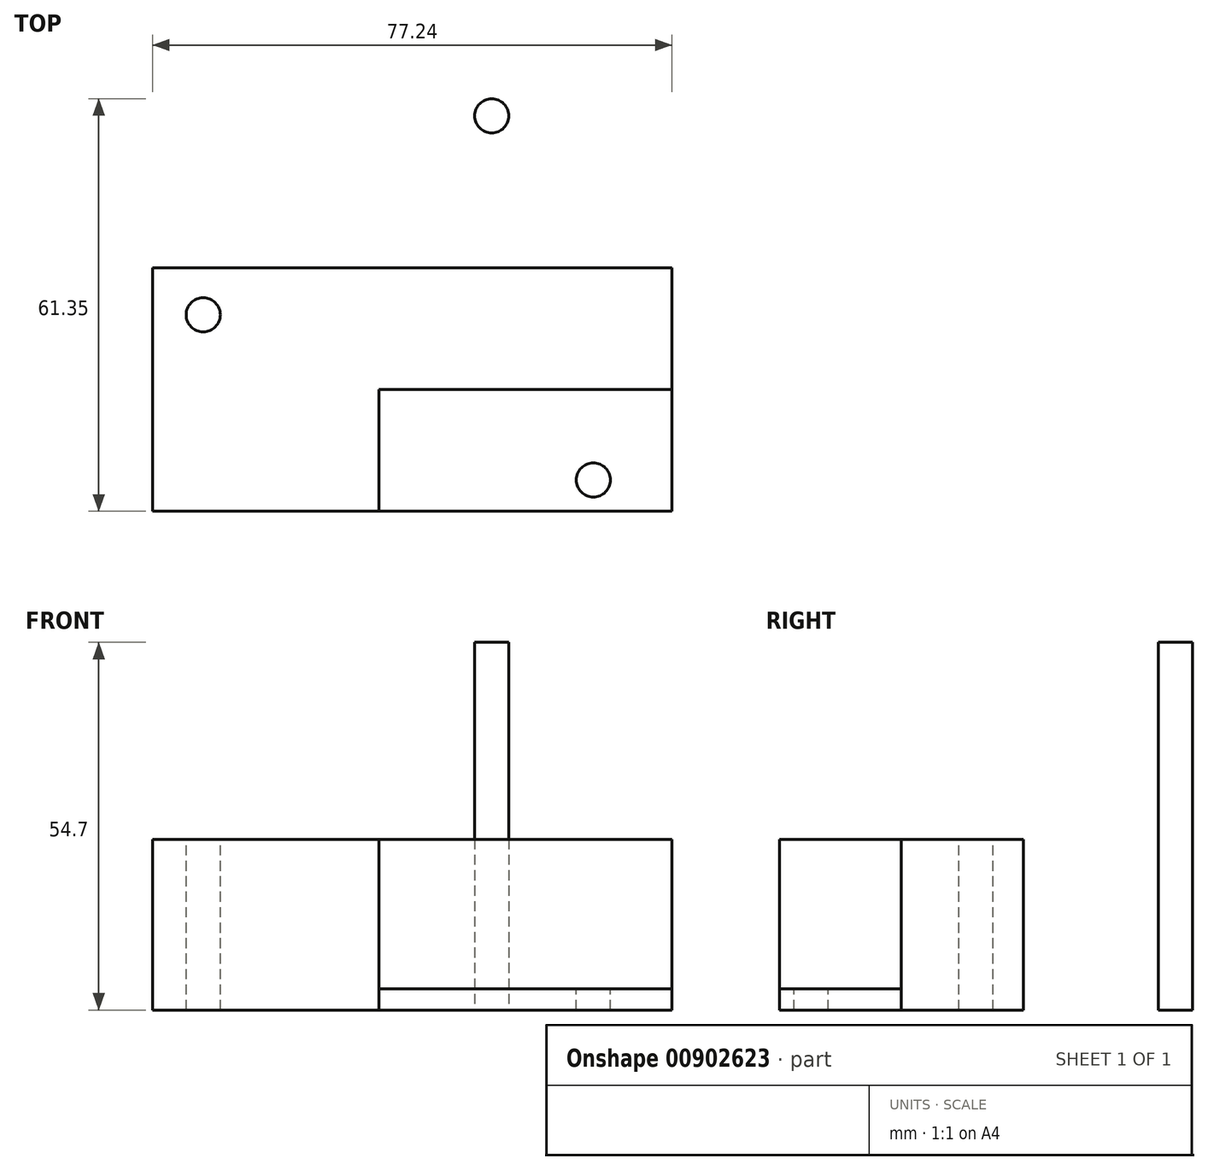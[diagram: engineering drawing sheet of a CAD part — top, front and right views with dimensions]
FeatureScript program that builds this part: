
annotation { "Feature Type Name" : "Feature", "Feature Type Description" : "" }
export const myFeature = defineFeature(function(context is Context, id is Id, definition is map)
    precondition{}
    {
        {
            var Q0;
            Q0=qCreatedBy(makeId("Top.planeOp"),FACE);
            var sketch = newSketch(context, id + "F0", { "sketchPlane" : qUnion([Q0])});
            skLineSegment(sketch, "E0.bottom", {"start": v(0, 0) * mm, "end": v(-77.24, 0) * mm});
            skLineSegment(sketch, "E0.top", {"start": v(0, 36.22) * mm, "end": v(-77.24, 36.22) * mm});
            skLineSegment(sketch, "E0.left", {"start": v(0, 0) * mm, "end": v(0, 36.22) * mm});
            skLineSegment(sketch, "E0.right", {"start": v(-77.24, 0) * mm, "end": v(-77.24, 36.22) * mm});
            skPoint(sketch, "E1.oppositeSnap0", {"position": v(0, 18.1) * mm});
            skLineSegment(sketch, "E1.bottom", {"start": v(0, 0) * mm, "end": v(-43.6, 0) * mm});
            skLineSegment(sketch, "E1.top", {"start": v(0, 18.1) * mm, "end": v(-43.6, 18.1) * mm});
            skLineSegment(sketch, "E1.left", {"start": v(0, 0) * mm, "end": v(0, 18.1) * mm});
            skLineSegment(sketch, "E1.right", {"start": v(-43.6, 0) * mm, "end": v(-43.6, 18.1) * mm});
            skSolve(sketch);
        }
        {
            var Q0;
            {var subQ2=sQuery(id+"F0.wireOp",EDGE,"E0.top");Q0=makeQuery(id+"F0.imprint","IMPRINT",FACE,{"disambiguationData":[TD([[makeQuery(id+"F0.imprint","IMPRINT",EDGE,{"derivedFrom":subQ2}),1.0]])]});}
            extrude(context, id + "F1", {"entities" : qUnion([Q0]), "depth" : 25.4 * mm, "offsetDistance" : 25.4 * mm});
        }
        {
            var Q0;
            {var subQ4=sQuery(id+"F0.wireOp",EDGE,"E1.top");Q0=makeQuery(id+"F0.imprint","IMPRINT",FACE,{"disambiguationData":[TD([[makeQuery(id+"F0.imprint","IMPRINT",EDGE,{"derivedFrom":subQ4}),1.0]])]});}
            extrude(context, id + "F2", {"entities" : qUnion([Q0]), "depth" : 3.12 * mm, "offsetDistance" : 25.4 * mm});
        }
        {
            var Q0;
            Q0=makeQuery(id+"F1.opExtrude","CAP_FACE",FACE,{"disambiguationData":[OSD([sQuery(id+"F0.wireOp",EDGE,"E0.bottom"),sQuery(id+"F0.wireOp",EDGE,"E0.top"),sQuery(id+"F0.wireOp",EDGE,"E0.left"),sQuery(id+"F0.wireOp",EDGE,"E0.right"),sQuery(id+"F0.wireOp",EDGE,"E1.top"),sQuery(id+"F0.wireOp",EDGE,"E1.right")])],"isStart":false});
            var sketch = newSketch(context, id + "F3", { "sketchPlane" : qUnion([Q0])});
            skCircle(sketch, "E2", {"center": v(-69.71, 29.21) * mm, "radius": 2.54 * mm});
            skSolve(sketch);
        }
        {
            var Q0;
            Q0=makeQuery(id+"F3.imprint","IMPRINT",FACE,{"disambiguationData":[TD([[makeQuery(id+"F3.imprint","IMPRINT",EDGE,{"derivedFrom":sQuery(id+"F3.wireOp",EDGE,"E2")}),-1.0]])]});
            var sketch = newSketch(context, id + "F4", { "sketchPlane" : qUnion([Q0])});
            skCircle(sketch, "E3", {"center": v(-11.7, 4.65) * mm, "radius": 2.54 * mm});
            skSolve(sketch);
        }
        {
            var Q0;
            Q0=qCreatedBy(makeId("Top.planeOp"),FACE);
            var sketch = newSketch(context, id + "F5", { "sketchPlane" : qUnion([Q0])});
            skCircle(sketch, "E4", {"center": v(-26.81, 58.81) * mm, "radius": 2.54 * mm});
            skSolve(sketch);
        }
        {
            var Q0;
            Q0=makeQuery(id+"F5.imprint","IMPRINT",FACE,{"disambiguationData":[TD([[makeQuery(id+"F5.imprint","IMPRINT",EDGE,{"derivedFrom":sQuery(id+"F5.wireOp",EDGE,"E4")}),1.0]])]});
            extrude(context, id + "F6", {"entities" : qUnion([Q0]), "depth" : 54.7 * mm, "offsetDistance" : 25.4 * mm});
        }
        {
            var Q0;
            Q0=makeQuery(id+"F4.imprint","IMPRINT",FACE,{"disambiguationData":[TD([[makeQuery(id+"F4.imprint","IMPRINT",EDGE,{"derivedFrom":sQuery(id+"F4.wireOp",EDGE,"E3")}),1.0]])]});
            extrude(context, id + "F7", {"entities" : qUnion([Q0]), "operationType" : NewBodyOperationType.REMOVE, "oppositeDirection" : true, "depth" : 47.64 * mm, "offsetDistance" : 25.4 * mm});
        }
        {
            var Q0;
            Q0=makeQuery(id+"F3.imprint","IMPRINT",FACE,{"disambiguationData":[TD([[makeQuery(id+"F3.imprint","IMPRINT",EDGE,{"derivedFrom":sQuery(id+"F3.wireOp",EDGE,"E2")}),1.0]])]});
            extrude(context, id + "F8", {"entities" : qUnion([Q0]), "operationType" : NewBodyOperationType.REMOVE, "oppositeDirection" : true, "depth" : 52.47 * mm, "offsetDistance" : 25.4 * mm});
        }
    });
